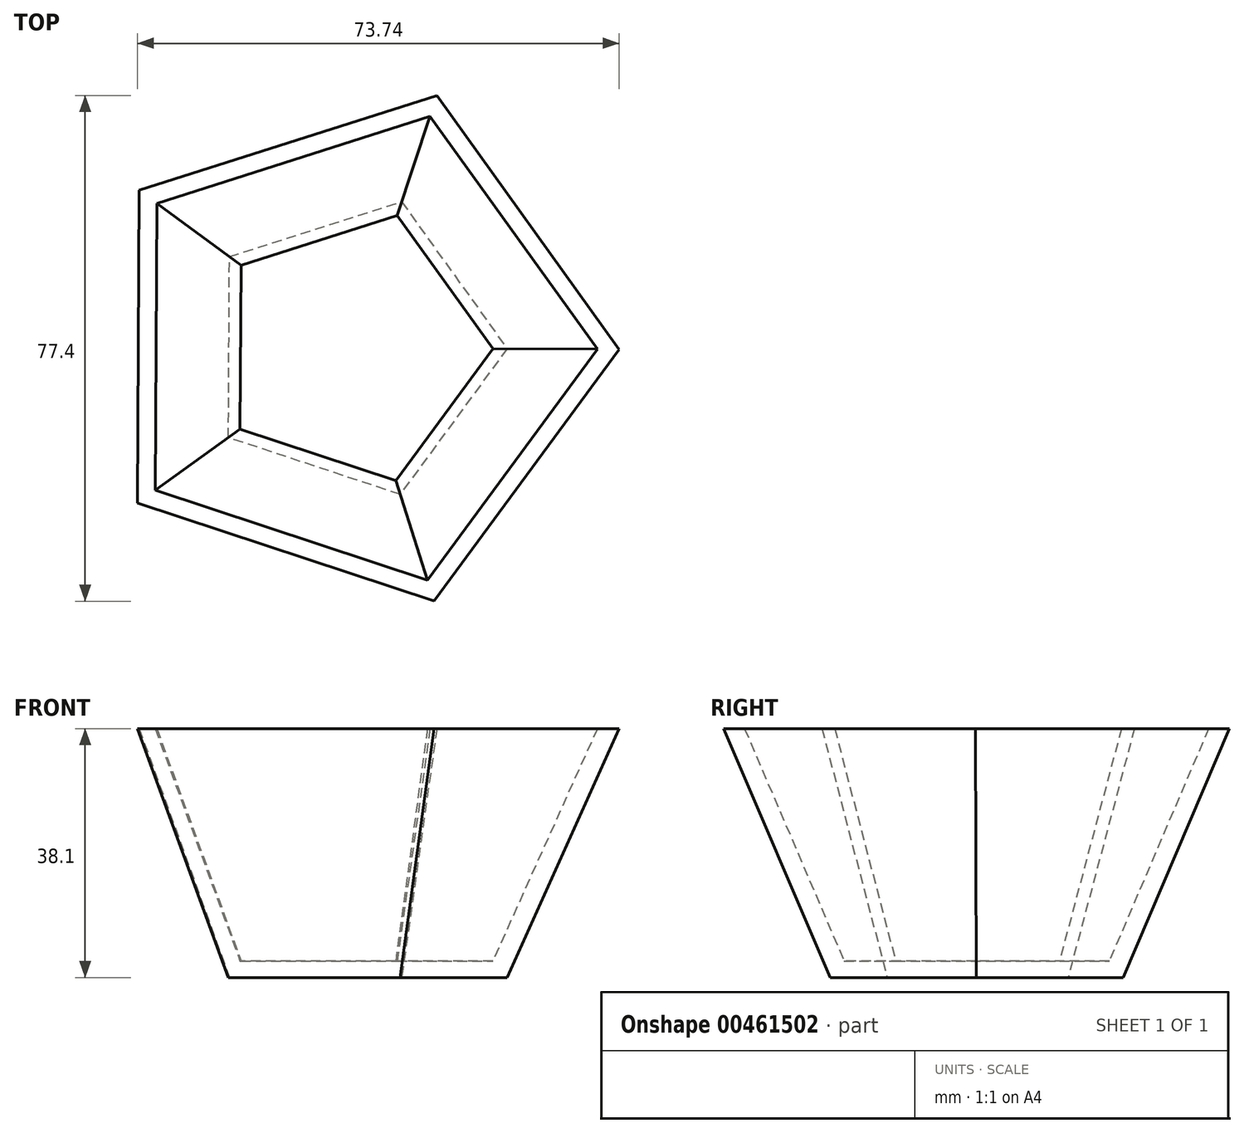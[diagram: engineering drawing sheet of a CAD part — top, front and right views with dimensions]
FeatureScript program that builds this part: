
annotation { "Feature Type Name" : "Feature", "Feature Type Description" : "" }
export const myFeature = defineFeature(function(context is Context, id is Id, definition is map)
    precondition{}
    {
        {
            var Q0;
            Q0=qCreatedBy(makeId("Top.planeOp"),FACE);
            var sketch = newSketch(context, id + "F0", { "sketchPlane" : qUnion([Q0])});
            skCircle(sketch, "E0.cCircle", {"center": v(0, 0) * mm, "radius": 19.05 * mm, "construction": true});
            skLineSegment(sketch, "E0.0", {"start": v(7.4, 22.35) * mm, "end": v(23.55, -0.13) * mm});
            skLineSegment(sketch, "E0.1", {"start": v(23.55, -0.13) * mm, "end": v(7.15, -22.43) * mm});
            skLineSegment(sketch, "E0.2", {"start": v(7.15, -22.43) * mm, "end": v(-19.13, -13.73) * mm});
            skLineSegment(sketch, "E0.3", {"start": v(-19.13, -13.73) * mm, "end": v(-18.97, 13.95) * mm});
            skLineSegment(sketch, "E0.4", {"start": v(-18.97, 13.95) * mm, "end": v(7.4, 22.35) * mm});
            skPoint(sketch, "E0.0.midPoint", {"position": v(15.47, 11.11) * mm});
            skSolve(sketch);
        }
        {
            var Q0;
            Q0=makeQuery(id+"F0.imprint","IMPRINT",FACE,{"disambiguationData":[TD([[makeQuery(id+"F0.imprint","IMPRINT",EDGE,{"derivedFrom":sQuery(id+"F0.wireOp",EDGE,"E0.0")}),-1.0]])]});
            extrude(context, id + "F1", {"entities" : qUnion([Q0]), "depth" : 38.1 * mm, "hasDraft" : true, "draftAngle" : 20 * degree});
        }
        {
            var Q0;
            Q0=makeQuery(id+"F1.opExtrude","CAP_FACE",FACE,{"disambiguationData":[OSD([sQuery(id+"F0.wireOp",EDGE,"E0.0"),sQuery(id+"F0.wireOp",EDGE,"E0.1"),sQuery(id+"F0.wireOp",EDGE,"E0.2"),sQuery(id+"F0.wireOp",EDGE,"E0.3"),sQuery(id+"F0.wireOp",EDGE,"E0.4")])],"isStart":false});
            shell(context, id + "F2", {"entities" : qUnion([Q0]), "thickness" : 2.54 * mm});
        }
    });
